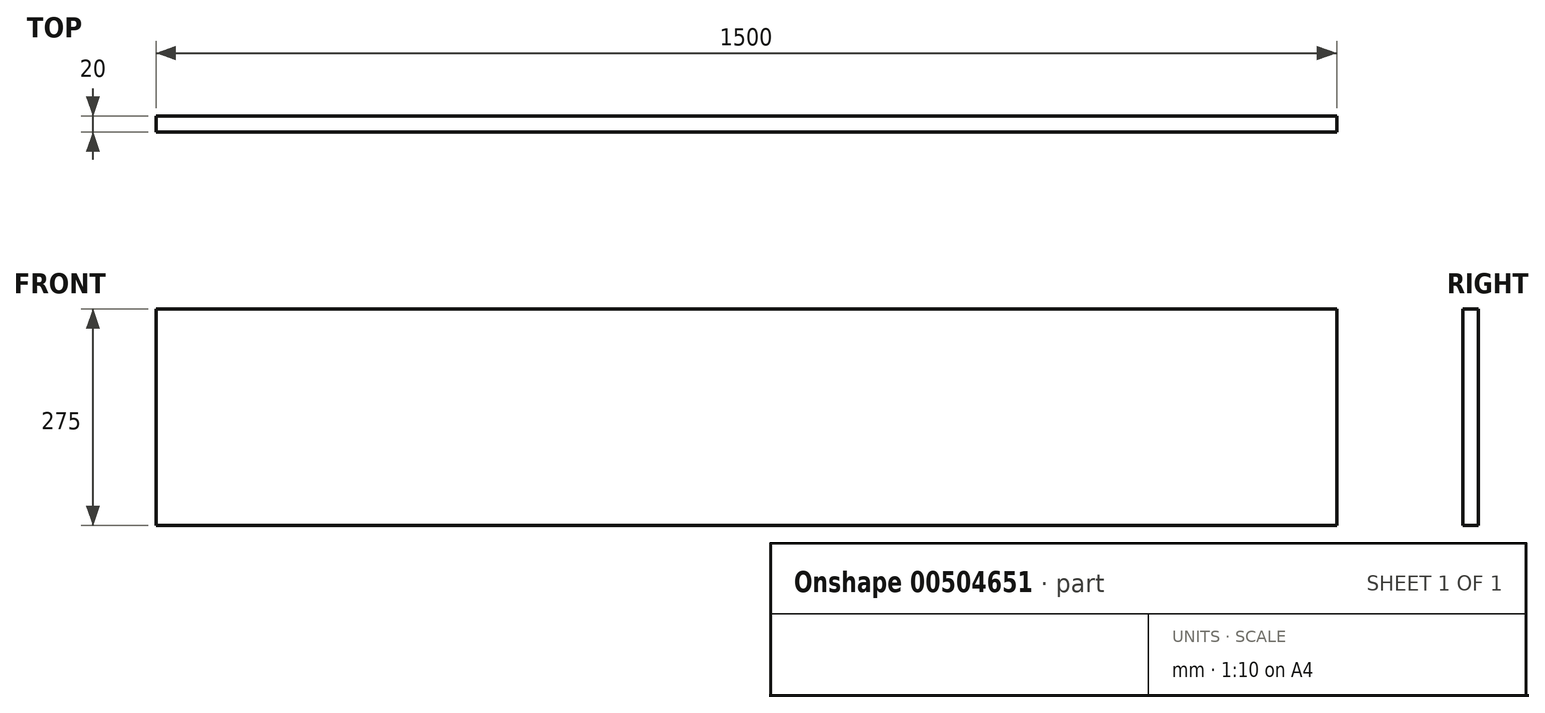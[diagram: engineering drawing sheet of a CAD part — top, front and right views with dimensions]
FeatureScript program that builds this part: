
annotation { "Feature Type Name" : "Feature", "Feature Type Description" : "" }
export const myFeature = defineFeature(function(context is Context, id is Id, definition is map)
    precondition{}
    {
        {
            var Q0;
            Q0=qCreatedBy(makeId("Front.planeOp"),FACE);
            var sketch = newSketch(context, id + "F0", { "sketchPlane" : qUnion([Q0])});
            skLineSegment(sketch, "E0.bottom", {"start": v(-141.9, 137.72) * mm, "end": v(1358.1, 137.72) * mm});
            skLineSegment(sketch, "E0.top", {"start": v(-141.9, -137.28) * mm, "end": v(1358.1, -137.28) * mm});
            skLineSegment(sketch, "E0.left", {"start": v(-141.9, 137.72) * mm, "end": v(-141.9, -137.28) * mm});
            skLineSegment(sketch, "E0.right", {"start": v(1358.1, 137.72) * mm, "end": v(1358.1, -137.28) * mm});
            skSolve(sketch);
        }
        {
            var Q0;
            Q0=makeQuery(id+"F0.imprint","IMPRINT",FACE,{"disambiguationData":[TD([[makeQuery(id+"F0.imprint","IMPRINT",EDGE,{"derivedFrom":sQuery(id+"F0.wireOp",EDGE,"E0.bottom")}),-1.0]])]});
            extrude(context, id + "F1", {"entities" : qUnion([Q0]), "depth" : 20 * mm});
        }
        {
            var Q0;
            Q0=makeQuery(id+"F1.opExtrude","CAP_FACE",FACE,{"disambiguationData":[OSD([sQuery(id+"F0.wireOp",EDGE,"E0.bottom"),sQuery(id+"F0.wireOp",EDGE,"E0.top"),sQuery(id+"F0.wireOp",EDGE,"E0.left"),sQuery(id+"F0.wireOp",EDGE,"E0.right")])],"isStart":false});
            var sketch = newSketch(context, id + "F2", { "sketchPlane" : qUnion([Q0])});
            skLineSegment(sketch, "E1", {"start": v(-141.9, 137.72) * mm, "end": v(-131.9, 137.72) * mm});
            skLineSegment(sketch, "E2", {"start": v(-131.9, 137.72) * mm, "end": v(-131.9, 87.72) * mm});
            skLineSegment(sketch, "E3", {"start": v(-131.9, 87.72) * mm, "end": v(-131.9, -87.28) * mm});
            skLineSegment(sketch, "E4", {"start": v(-131.9, -87.28) * mm, "end": v(-131.9, -137.28) * mm});
            skPoint(sketch, "E5", {"position": v(608.1, 137.72) * mm});
            skLineSegment(sketch, "E6", {"start": v(608.1, 137.72) * mm, "end": v(608.1, 87.72) * mm});
            skLineSegment(sketch, "E7", {"start": v(608.1, 87.72) * mm, "end": v(608.1, -87.28) * mm});
            skLineSegment(sketch, "E8", {"start": v(608.1, -87.28) * mm, "end": v(608.1, -122.28) * mm});
            skLineSegment(sketch, "E9.MirrorCS", {"start": v(1348.1, 137.72) * mm, "end": v(1348.1, 87.72) * mm});
            skLineSegment(sketch, "E10.MirrorCS", {"start": v(1348.1, 87.72) * mm, "end": v(1348.1, -87.28) * mm});
            skLineSegment(sketch, "E11.MirrorCS", {"start": v(1348.1, -87.28) * mm, "end": v(1348.1, -137.28) * mm});
            skLineSegment(sketch, "E12", {"start": v(608.1, -137.28) * mm, "end": v(608.1, -122.28) * mm});
            skLineSegment(sketch, "E13", {"start": v(608.1, -122.28) * mm, "end": v(608.1, -137.28) * mm});
            skSolve(sketch);
        }
    });
